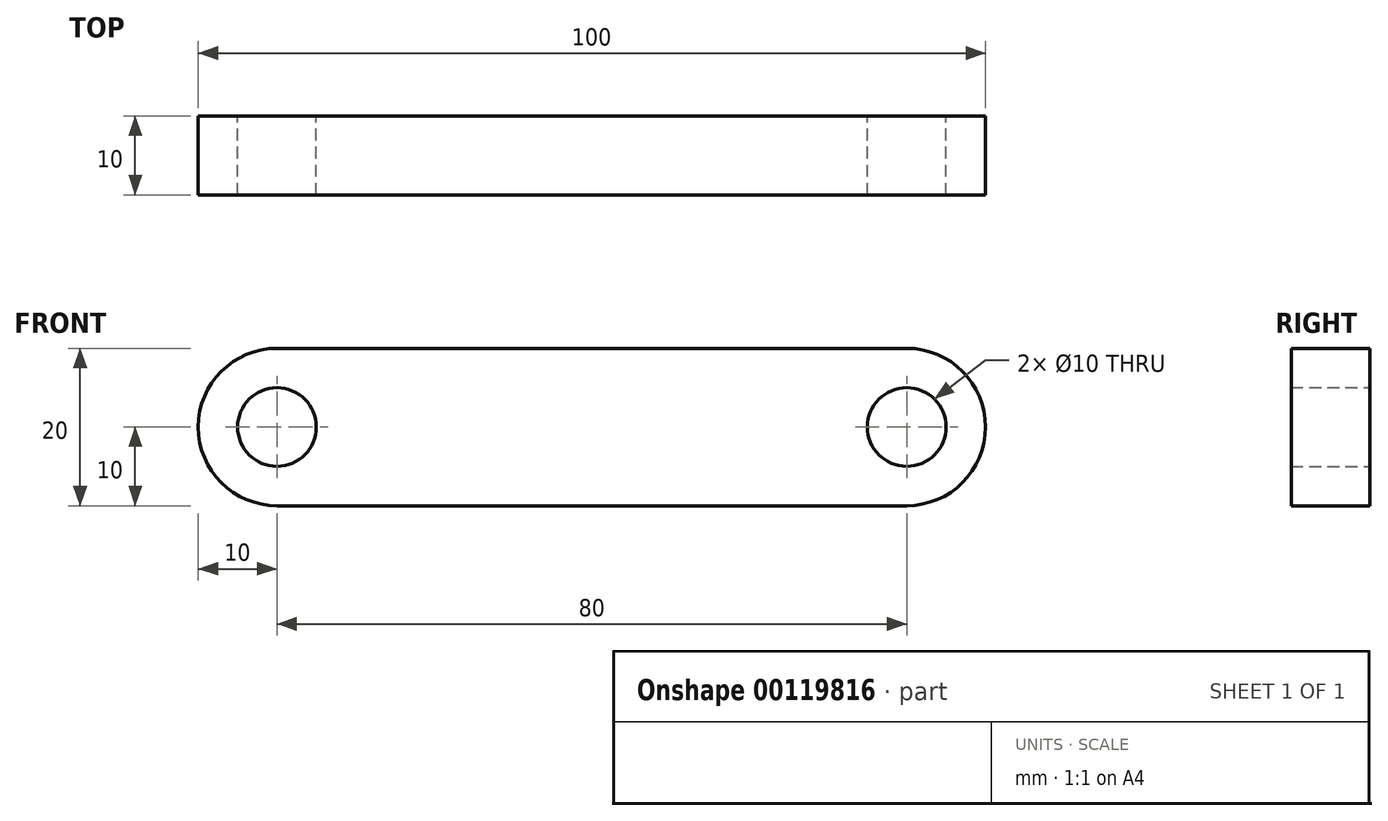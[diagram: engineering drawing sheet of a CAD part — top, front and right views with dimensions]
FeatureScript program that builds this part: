
annotation { "Feature Type Name" : "Feature", "Feature Type Description" : "" }
export const myFeature = defineFeature(function(context is Context, id is Id, definition is map)
    precondition{}
    {
        {
            var Q0;
            Q0=qCreatedBy(makeId("Front.planeOp"),FACE);
            var sketch = newSketch(context, id + "F0", { "sketchPlane" : qUnion([Q0])});
            skArc(sketch, "E0", {"start": v(0, 20) * mm, "mid": v(-10, 10) * mm, "end": v(0, 0) * mm});
            skArc(sketch, "E1", {"start": v(80, 0) * mm, "mid": v(90, 10) * mm, "end": v(80, 20) * mm});
            skLineSegment(sketch, "E2", {"start": v(0, 20) * mm, "end": v(80, 20) * mm});
            skLineSegment(sketch, "E3", {"start": v(0, 0) * mm, "end": v(80, 0) * mm});
            skCircle(sketch, "E4", {"center": v(0, 10) * mm, "radius": 5 * mm});
            skCircle(sketch, "E5", {"center": v(80, 10) * mm, "radius": 5 * mm});
            skSolve(sketch);
        }
        {
            var Q0;
            Q0 = qSketchRegion(id + "F0", true);
            extrude(context, id + "F1", {"entities" : qUnion([Q0]), "depth" : 10 * mm});
        }
    });
